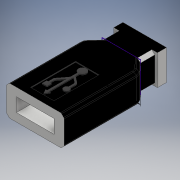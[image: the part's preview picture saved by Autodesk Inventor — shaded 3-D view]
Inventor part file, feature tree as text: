
AUTODESK INVENTOR PART (.ipt)
format: ipt  version: 2018 (Build 220112000, 112)  size: 348,160 bytes
history: native  units: mm
features: sketch x9, extrude x6, fillet x3, chamfer x2, plane x1
ambient origin geometry x8: Origin, YZ Plane, XZ Plane, XY Plane, X Axis, Y Axis, Z Axis, Center Point
bodies: Solid1 (feature_tree)
feature tree (21):
  extrude  "Extrusion1"  Depth=25.0mm
  chamfer  "Chamfer1"  Distance=10.0mm
  fillet  "Fillet1"  Radius=0.5mm
  fillet  "Fillet2"  Radius=3.0mm
  fillet  "Fillet3"  Radius=3.0mm
  extrude  "Extrusion2"  Depth=14.9mm
  extrude  "Extrusion7"  Depth=0.3mm TaperAngle=0.0deg
  plane  "Work Plane1"
  extrude  "Extrusion14"  Depth=12.5mm
  sketch  "Sketch18"  dims[d14=7.75mm d15=14.9mm]
  sketch  "Sketch19"  dims[d16=2.3mm d17=0.3mm d18=0.0mm]
  sketch  "Sketch20"  dims[d71=0.3mm d72=0.0mm d101=12.5mm]
  extrude  "Extrusion15"  Depth=20.0mm TaperAngle=0.0deg
  chamfer  "Chamfer2"  Distance=12.75mm
  sketch  "Sketch22"  dims[d102=4.52mm d106=20.0mm d107=0.0mm]
  extrude  "Extrusion17"  Depth=3.0mm TaperAngle=0.0deg
  sketch  "Sketch1"  dims[d2=19.05mm d3=25.0mm]
  sketch  "Sketch2"  dims[d4=12.75mm]
  sketch  "Sketch8"  dims[d5=3.4mm d6=10.0mm d7=0.0mm]
  sketch  "Sketch17"  dims[d8=1.0mm d9=2.0mm d10=45.0deg d11=0.5mm d12=3.0mm d13=3.0mm]
  sketch  "Sketch23"  dims[d108=2.26mm d109=12.75mm d110=4.77mm d111=0.0mm d112=1.0mm d113=2.0mm d114=45.0deg d118=14.42mm d119=10.0mm d120=3.0mm d121=0.0mm]
